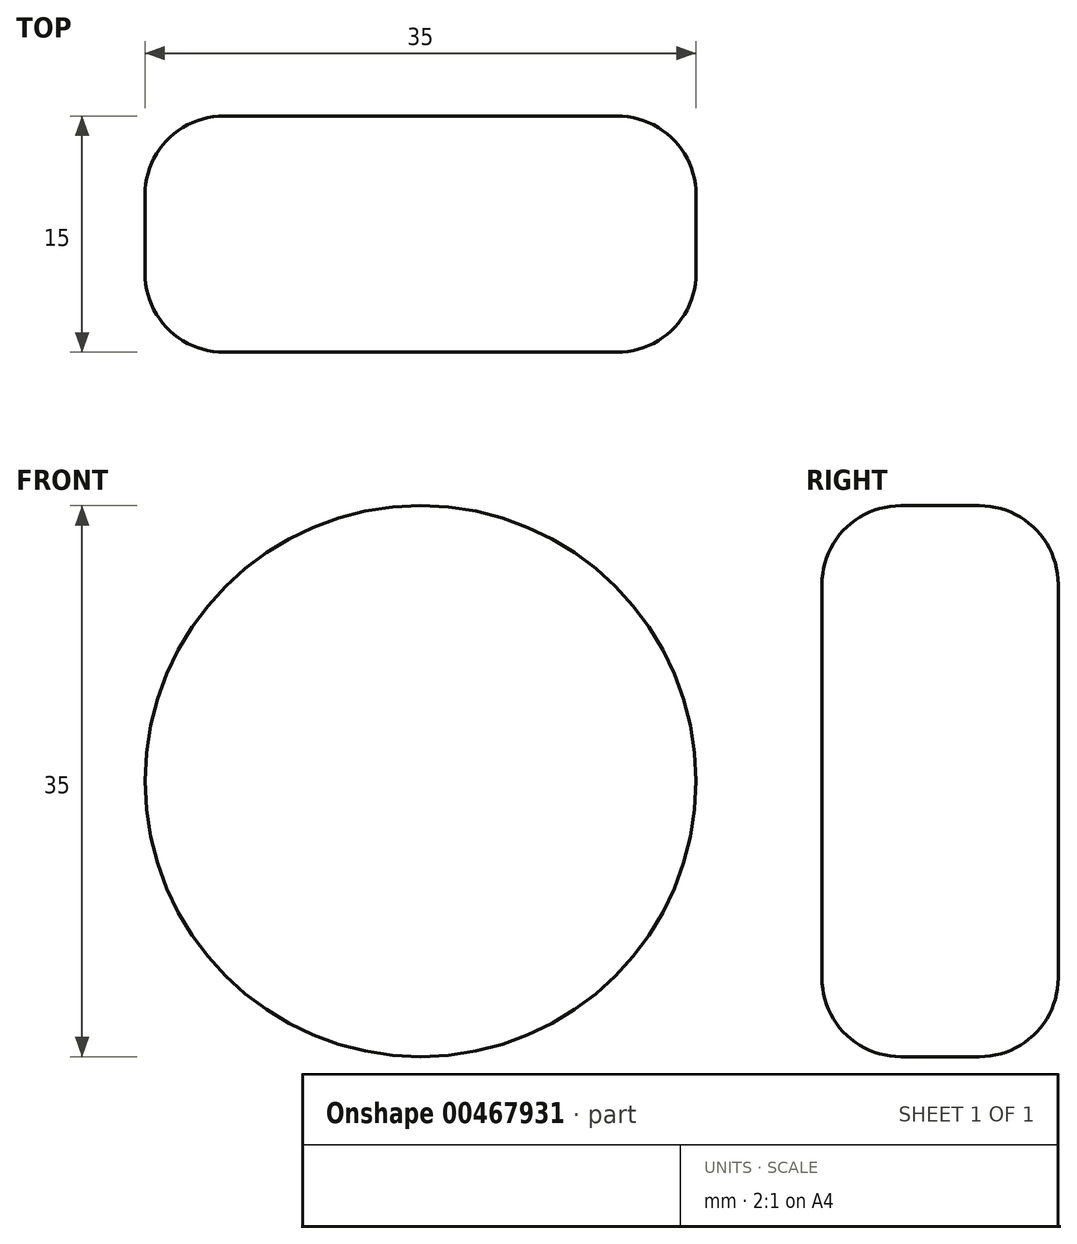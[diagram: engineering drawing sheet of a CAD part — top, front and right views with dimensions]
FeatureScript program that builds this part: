
annotation { "Feature Type Name" : "Feature", "Feature Type Description" : "" }
export const myFeature = defineFeature(function(context is Context, id is Id, definition is map)
    precondition{}
    {
        {
            var Q0;
            Q0=qCreatedBy(makeId("Front.planeOp"),FACE);
            var sketch = newSketch(context, id + "F0", { "sketchPlane" : qUnion([Q0])});
            skCircle(sketch, "E0", {"center": v(0, -3.5) * mm, "radius": 17.5 * mm});
            skPoint(sketch, "E1", {"position": v(0, 14) * mm});
            skPoint(sketch, "E2", {"position": v(-17.5, -3.5) * mm});
            skPoint(sketch, "E3", {"position": v(17.5, -3.5) * mm});
            skLineSegment(sketch, "E4", {"start": v(-17.5, -3.5) * mm, "end": v(17.5, -3.5) * mm});
            skSolve(sketch);
        }
        {
            var Q0;
            Q0 = qSketchRegion(id + "F0", true);
            extrude(context, id + "F1", {"entities" : qUnion([Q0]), "endBound" : BoundingType.SYMMETRIC, "oppositeDirection" : true, "depth" : 15 * mm});
        }
        {
            var Q0;
            Q0=makeQuery(id+"F1.opExtrude","SWEPT_FACE",FACE,{"disambiguationData":[OSD([sQuery(id+"F0.wireOp",EDGE,"E0")])]});
            fillet(context, id + "F2", {"entities" : qUnion([Q0]), "radius" : 5 * mm, "tangentPropagation" : true, "allowEdgeOverflow" : false});
        }
    });
